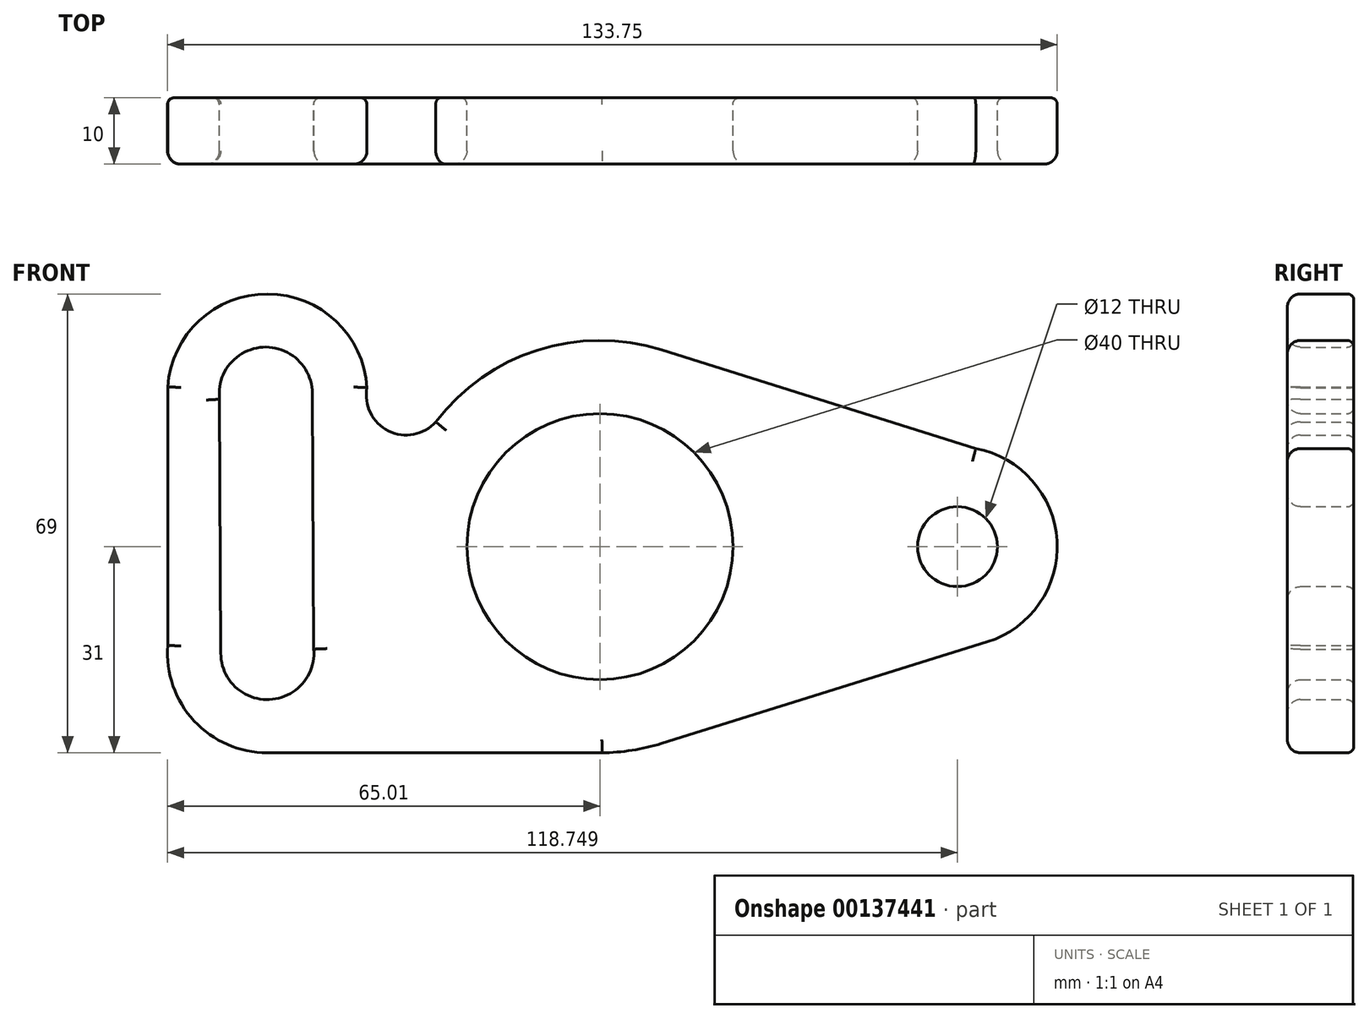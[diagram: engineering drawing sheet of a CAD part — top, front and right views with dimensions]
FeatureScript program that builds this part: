
annotation { "Feature Type Name" : "Feature", "Feature Type Description" : "" }
export const myFeature = defineFeature(function(context is Context, id is Id, definition is map)
    precondition{}
    {
        {
            var Q0;
            Q0=qCreatedBy(makeId("Front.planeOp"),FACE);
            var sketch = newSketch(context, id + "F3", { "sketchPlane" : qUnion([Q0])});
            skLineSegment(sketch, "E0", {"start": v(-102.47, 0) * mm, "end": v(109.99, 0) * mm, "construction": true});
            skLineSegment(sketch, "E1", {"start": v(0, 82.61) * mm, "end": v(0, -86.03) * mm, "construction": true});
            skSolve(sketch);
        }
        {
            var Q0;
            Q0=qCreatedBy(makeId("Front.planeOp"),FACE);
            var sketch = newSketch(context, id + "F0", { "sketchPlane" : qUnion([Q0])});
            skCircle(sketch, "E2", {"center": v(0, 0) * mm, "radius": 20 * mm});
            skCircle(sketch, "E3", {"center": v(53.74, 0) * mm, "radius": 6 * mm});
            skArc(sketch, "E4", {"start": v(58.2, -14.32) * mm, "mid": v(68.71, 0.88) * mm, "end": v(56.5, 14.75) * mm});
            skArc(sketch, "E5", {"start": v(-0.3, -31) * mm, "mid": v(4.52, -30.67) * mm, "end": v(9.23, -29.6) * mm});
            skArc(sketch, "E6", {"start": v(-57, -16.03) * mm, "mid": v(-49.7, -23) * mm, "end": v(-43.02, -15.41) * mm});
            skArc(sketch, "E7", {"start": v(-43.24, 23.04) * mm, "mid": v(-50.67, 29.99) * mm, "end": v(-57.18, 22.16) * mm});
            skLineSegment(sketch, "E8", {"start": v(-50, -16) * mm, "end": v(-50, 23) * mm});
            skArc(sketch, "E9", {"start": v(-35.05, 21.8) * mm, "mid": v(-49.9, 38) * mm, "end": v(-64.97, 22) * mm});
            skArc(sketch, "E10", {"start": v(-35.03, 23.9) * mm, "mid": v(-31.8, 17.4) * mm, "end": v(-24.68, 18.75) * mm});
            skLineSegment(sketch, "E11", {"start": v(9.23, -29.6) * mm, "end": v(58.2, -14.32) * mm});
            skLineSegment(sketch, "E12", {"start": v(56.5, 14.75) * mm, "end": v(9.3, 29.57) * mm});
            skLineSegment(sketch, "E13", {"start": v(-64.97, 24) * mm, "end": v(-64.97, -14.85) * mm});
            skLineSegment(sketch, "E14", {"start": v(-50, -31) * mm, "end": v(0.3, -31) * mm});
            skLineSegment(sketch, "E15", {"start": v(-43.02, -16.5) * mm, "end": v(-43.24, 23.04) * mm});
            skLineSegment(sketch, "E16", {"start": v(-57.18, 22.16) * mm, "end": v(-57, -16.03) * mm});
            skArc(sketch, "E17.trimOffspring", {"start": v(-64.97, -14.85) * mm, "mid": v(-61.01, -26.2) * mm, "end": v(-50, -31) * mm});
            skArc(sketch, "E18.trimOffspring", {"start": v(9.3, 29.57) * mm, "mid": v(-9.4, 29.54) * mm, "end": v(-24.68, 18.75) * mm});
            skSolve(sketch);
        }
        {
            var Q0;
            Q0=makeQuery(id+"F0.imprint","IMPRINT",FACE,{"disambiguationData":[TD([[makeQuery(id+"F0.imprint","IMPRINT",EDGE,{"derivedFrom":sQuery(id+"F0.wireOp",EDGE,"E2")}),-1.0]])]});
            extrude(context, id + "F4", {"entities" : qUnion([Q0]), "depth" : 10 * mm});
        }
        {
            var Q0;
            Q0=makeQuery(id+"F4.opExtrude","CAP_FACE",FACE,{"disambiguationData":[OSD([sQuery(id+"F0.wireOp",EDGE,"E2"),sQuery(id+"F0.wireOp",EDGE,"E3"),sQuery(id+"F0.wireOp",EDGE,"E4"),sQuery(id+"F0.wireOp",EDGE,"E5"),sQuery(id+"F0.wireOp",EDGE,"E6"),sQuery(id+"F0.wireOp",EDGE,"E7"),sQuery(id+"F0.wireOp",EDGE,"E9"),sQuery(id+"F0.wireOp",EDGE,"E10"),sQuery(id+"F0.wireOp",EDGE,"E11"),sQuery(id+"F0.wireOp",EDGE,"E12"),sQuery(id+"F0.wireOp",EDGE,"E13"),sQuery(id+"F0.wireOp",EDGE,"E14"),sQuery(id+"F0.wireOp",EDGE,"E15"),sQuery(id+"F0.wireOp",EDGE,"E16"),sQuery(id+"F0.wireOp",EDGE,"E17.trimOffspring"),sQuery(id+"F0.wireOp",EDGE,"E18.trimOffspring")])],"isStart":false});
            fillet(context, id + "F1", {"entities" : qUnion([Q0]), "radius" : 2 * mm, "tangentPropagation" : true, "allowEdgeOverflow" : false});
        }
        {
            var Q0;
            Q0=makeQuery(id+"F4.opExtrude","CAP_FACE",FACE,{"disambiguationData":[OSD([sQuery(id+"F0.wireOp",EDGE,"E2"),sQuery(id+"F0.wireOp",EDGE,"E3"),sQuery(id+"F0.wireOp",EDGE,"E4"),sQuery(id+"F0.wireOp",EDGE,"E5"),sQuery(id+"F0.wireOp",EDGE,"E6"),sQuery(id+"F0.wireOp",EDGE,"E7"),sQuery(id+"F0.wireOp",EDGE,"E9"),sQuery(id+"F0.wireOp",EDGE,"E10"),sQuery(id+"F0.wireOp",EDGE,"E11"),sQuery(id+"F0.wireOp",EDGE,"E12"),sQuery(id+"F0.wireOp",EDGE,"E13"),sQuery(id+"F0.wireOp",EDGE,"E14"),sQuery(id+"F0.wireOp",EDGE,"E15"),sQuery(id+"F0.wireOp",EDGE,"E16"),sQuery(id+"F0.wireOp",EDGE,"E17.trimOffspring"),sQuery(id+"F0.wireOp",EDGE,"E18.trimOffspring")])],"isStart":true});
            fillet(context, id + "F2", {"entities" : qUnion([Q0]), "radius" : 1 * mm, "tangentPropagation" : true, "allowEdgeOverflow" : false});
        }
    });
